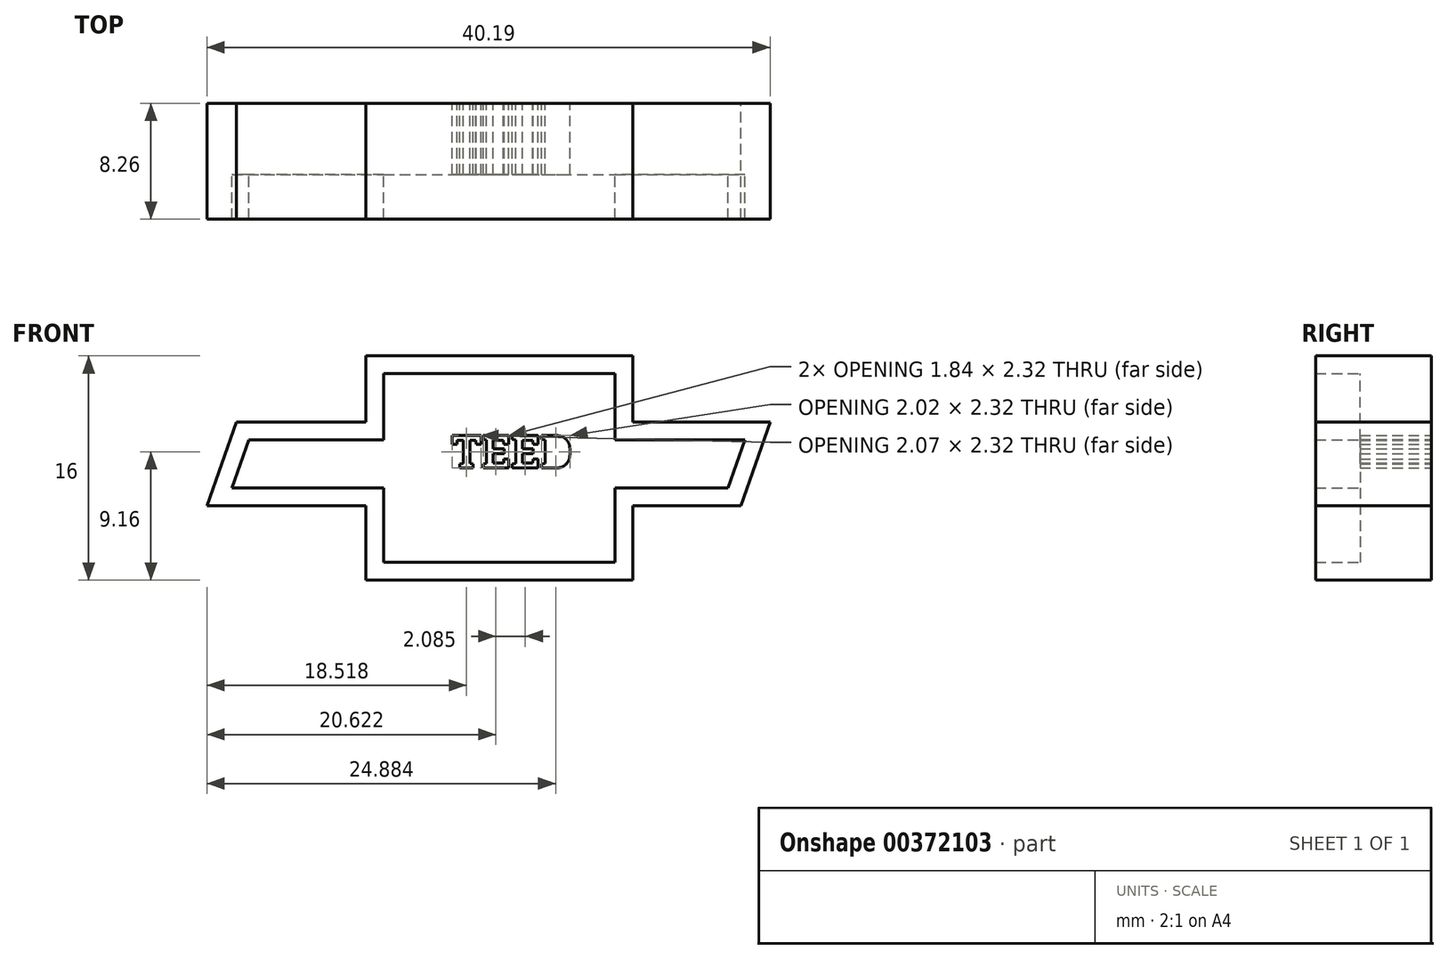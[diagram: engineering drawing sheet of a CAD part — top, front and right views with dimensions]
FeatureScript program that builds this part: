
annotation { "Feature Type Name" : "Feature", "Feature Type Description" : "" }
export const myFeature = defineFeature(function(context is Context, id is Id, definition is map)
    precondition{}
    {
        {
            var Q0;
            Q0=qCreatedBy(makeId("Front.planeOp"),FACE);
            var sketch = newSketch(context, id + "F0", { "sketchPlane" : qUnion([Q0])});
            skLineSegment(sketch, "E0.bottom", {"start": v(-9.53, 8) * mm, "end": v(9.53, 8) * mm});
            skLineSegment(sketch, "E0.top", {"start": v(-9.53, -8) * mm, "end": v(9.53, -8) * mm});
            skLineSegment(sketch, "E0.left", {"start": v(-9.53, 8) * mm, "end": v(-9.53, 3.29) * mm});
            skLineSegment(sketch, "E0.right", {"start": v(9.53, 8) * mm, "end": v(9.53, 3.29) * mm});
            skPoint(sketch, "E0.middle", {"position": v(0, 0) * mm});
            skLineSegment(sketch, "E1", {"start": v(-19.33, -3.29) * mm, "end": v(-20.86, -2.7) * mm});
            skLineSegment(sketch, "E2", {"start": v(-20.86, -2.7) * mm, "end": v(-18.77, 3.29) * mm});
            skLineSegment(sketch, "E3", {"start": v(19.33, 3.29) * mm, "end": v(17.24, -2.7) * mm});
            skPoint(sketch, "E4.orphan", {"position": v(18.77, -3.29) * mm});
            skLineSegment(sketch, "E5", {"start": v(-18.77, 3.29) * mm, "end": v(-9.53, 3.29) * mm});
            skLineSegment(sketch, "E6", {"start": v(-20.86, -2.7) * mm, "end": v(-9.53, -2.7) * mm});
            skText(sketch, "E7", { "text": "TEED", "fontName": "RobotoSlab-Bold.ttf"});
            skLineSegment(sketch, "E8.trimOffspring", {"start": v(-9.53, -2.7) * mm, "end": v(-9.53, -8) * mm});
            skLineSegment(sketch, "E9.trimOffspring", {"start": v(9.53, 3.29) * mm, "end": v(19.33, 3.29) * mm});
            skLineSegment(sketch, "E10.trimOffspring", {"start": v(9.53, -2.7) * mm, "end": v(17.24, -2.7) * mm});
            skLineSegment(sketch, "E11.trimOffspring", {"start": v(9.53, -2.7) * mm, "end": v(9.53, -8) * mm});
            const initialGuessF0  = {"E7": [-0.00344, 0, 1, 0, 0.00235]};
            skSetInitialGuess(sketch, initialGuessF0);
            skSolve(sketch);
        }
        {
            var Q0;
            Q0 = qSketchRegion(id + "F0", true);
            extrude(context, id + "F1", {"entities" : qUnion([Q0]), "depth" : 5.08 * mm});
        }
        {
            var Q0;
            Q0=makeQuery(id+"F1.opExtrude","CAP_FACE",FACE,{"disambiguationData":[OSD([sQuery(id+"F0.wireOp",EDGE,"E0.bottom"),sQuery(id+"F0.wireOp",EDGE,"E0.top"),sQuery(id+"F0.wireOp",EDGE,"E0.left"),sQuery(id+"F0.wireOp",EDGE,"E0.right"),sQuery(id+"F0.wireOp",EDGE,"E2"),sQuery(id+"F0.wireOp",EDGE,"E3"),sQuery(id+"F0.wireOp",EDGE,"E5"),sQuery(id+"F0.wireOp",EDGE,"E6"),sQuery(id+"F0.wireOp",EDGE,"E7.sketch_text.stroke-0"),sQuery(id+"F0.wireOp",EDGE,"E7.sketch_text.stroke-1"),sQuery(id+"F0.wireOp",EDGE,"E7.sketch_text.stroke-2"),sQuery(id+"F0.wireOp",EDGE,"E7.sketch_text.stroke-3"),sQuery(id+"F0.wireOp",EDGE,"E7.sketch_text.stroke-4"),sQuery(id+"F0.wireOp",EDGE,"E7.sketch_text.stroke-5"),sQuery(id+"F0.wireOp",EDGE,"E7.sketch_text.stroke-6"),sQuery(id+"F0.wireOp",EDGE,"E7.sketch_text.stroke-7"),sQuery(id+"F0.wireOp",EDGE,"E7.sketch_text.stroke-8"),sQuery(id+"F0.wireOp",EDGE,"E7.sketch_text.stroke-9"),sQuery(id+"F0.wireOp",EDGE,"E7.sketch_text.stroke-10"),sQuery(id+"F0.wireOp",EDGE,"E7.sketch_text.stroke-11"),sQuery(id+"F0.wireOp",EDGE,"E7.sketch_text.stroke-12"),sQuery(id+"F0.wireOp",EDGE,"E7.sketch_text.stroke-13"),sQuery(id+"F0.wireOp",EDGE,"E7.sketch_text.stroke-14"),sQuery(id+"F0.wireOp",EDGE,"E7.sketch_text.stroke-15"),sQuery(id+"F0.wireOp",EDGE,"E7.sketch_text.stroke-16"),sQuery(id+"F0.wireOp",EDGE,"E7.sketch_text.stroke-17"),sQuery(id+"F0.wireOp",EDGE,"E7.sketch_text.stroke-18"),sQuery(id+"F0.wireOp",EDGE,"E7.sketch_text.stroke-19"),sQuery(id+"F0.wireOp",EDGE,"E7.sketch_text.stroke-20"),sQuery(id+"F0.wireOp",EDGE,"E7.sketch_text.stroke-21"),sQuery(id+"F0.wireOp",EDGE,"E7.sketch_text.stroke-22"),sQuery(id+"F0.wireOp",EDGE,"E7.sketch_text.stroke-23"),sQuery(id+"F0.wireOp",EDGE,"E7.sketch_text.stroke-24"),sQuery(id+"F0.wireOp",EDGE,"E7.sketch_text.stroke-25"),sQuery(id+"F0.wireOp",EDGE,"E7.sketch_text.stroke-26"),sQuery(id+"F0.wireOp",EDGE,"E7.sketch_text.stroke-27"),sQuery(id+"F0.wireOp",EDGE,"E7.sketch_text.stroke-28"),sQuery(id+"F0.wireOp",EDGE,"E7.sketch_text.stroke-29"),sQuery(id+"F0.wireOp",EDGE,"E7.sketch_text.stroke-30"),sQuery(id+"F0.wireOp",EDGE,"E7.sketch_text.stroke-31"),sQuery(id+"F0.wireOp",EDGE,"E7.sketch_text.stroke-32"),sQuery(id+"F0.wireOp",EDGE,"E7.sketch_text.stroke-33"),sQuery(id+"F0.wireOp",EDGE,"E7.sketch_text.stroke-34"),sQuery(id+"F0.wireOp",EDGE,"E7.sketch_text.stroke-35"),sQuery(id+"F0.wireOp",EDGE,"E7.sketch_text.stroke-36"),sQuery(id+"F0.wireOp",EDGE,"E7.sketch_text.stroke-37"),sQuery(id+"F0.wireOp",EDGE,"E7.sketch_text.stroke-38"),sQuery(id+"F0.wireOp",EDGE,"E8.trimOffspring"),sQuery(id+"F0.wireOp",EDGE,"E9.trimOffspring"),sQuery(id+"F0.wireOp",EDGE,"E10.trimOffspring"),sQuery(id+"F0.wireOp",EDGE,"E11.trimOffspring")])],"isStart":false});
            var sketch = newSketch(context, id + "F2", { "sketchPlane" : qUnion([Q0])});
            skLineSegment(sketch, "E12", {"start": v(-18.77, 3.29) * mm, "end": v(-20.86, -2.7) * mm});
            skLineSegment(sketch, "E13", {"start": v(-20.86, -2.7) * mm, "end": v(-9.53, -2.7) * mm});
            skLineSegment(sketch, "E14", {"start": v(-9.53, -2.7) * mm, "end": v(-9.53, -8) * mm});
            skLineSegment(sketch, "E15", {"start": v(-9.53, -8) * mm, "end": v(9.53, -8) * mm});
            skLineSegment(sketch, "E16", {"start": v(9.53, -8) * mm, "end": v(9.53, -2.7) * mm});
            skLineSegment(sketch, "E17", {"start": v(9.53, -2.7) * mm, "end": v(17.24, -2.7) * mm});
            skLineSegment(sketch, "E18", {"start": v(17.24, -2.7) * mm, "end": v(19.33, 3.29) * mm});
            skLineSegment(sketch, "E19", {"start": v(19.33, 3.29) * mm, "end": v(9.53, 3.29) * mm});
            skLineSegment(sketch, "E20", {"start": v(9.53, 3.29) * mm, "end": v(9.53, 8) * mm});
            skLineSegment(sketch, "E21", {"start": v(9.53, 8) * mm, "end": v(-9.53, 8) * mm});
            skLineSegment(sketch, "E22", {"start": v(-9.53, 8) * mm, "end": v(-9.53, 3.29) * mm});
            skLineSegment(sketch, "E23", {"start": v(-9.53, 3.29) * mm, "end": v(-18.77, 3.29) * mm});
            skLineSegment(sketch, "E24.0", {"start": v(8.25, 2.02) * mm, "end": v(8.25, 6.73) * mm});
            skLineSegment(sketch, "E24.1", {"start": v(-19.08, -1.44) * mm, "end": v(-8.25, -1.44) * mm});
            skLineSegment(sketch, "E24.2", {"start": v(-17.87, 2.02) * mm, "end": v(-19.08, -1.44) * mm});
            skLineSegment(sketch, "E24.3", {"start": v(-8.25, 2.02) * mm, "end": v(-17.87, 2.02) * mm});
            skLineSegment(sketch, "E24.4", {"start": v(-8.25, 6.73) * mm, "end": v(-8.25, 2.02) * mm});
            skLineSegment(sketch, "E24.5", {"start": v(-8.25, -1.44) * mm, "end": v(-8.25, -6.73) * mm});
            skLineSegment(sketch, "E24.6", {"start": v(8.25, 6.73) * mm, "end": v(-8.25, 6.73) * mm});
            skLineSegment(sketch, "E24.7", {"start": v(-8.25, -6.73) * mm, "end": v(8.25, -6.73) * mm});
            skLineSegment(sketch, "E24.8", {"start": v(8.25, -6.73) * mm, "end": v(8.25, -1.44) * mm});
            skLineSegment(sketch, "E24.9", {"start": v(8.25, -1.44) * mm, "end": v(16.33, -1.44) * mm});
            skLineSegment(sketch, "E24.10", {"start": v(16.33, -1.44) * mm, "end": v(17.54, 2.02) * mm});
            skLineSegment(sketch, "E24.11", {"start": v(17.54, 2.02) * mm, "end": v(8.25, 2.02) * mm});
            skSolve(sketch);
        }
        {
            var Q0;
            Q0 = qSketchRegion(id + "F2", true);
            extrude(context, id + "F3", {"entities" : qUnion([Q0]), "operationType" : NewBodyOperationType.ADD, "depth" : 3.17 * mm});
        }
    });
